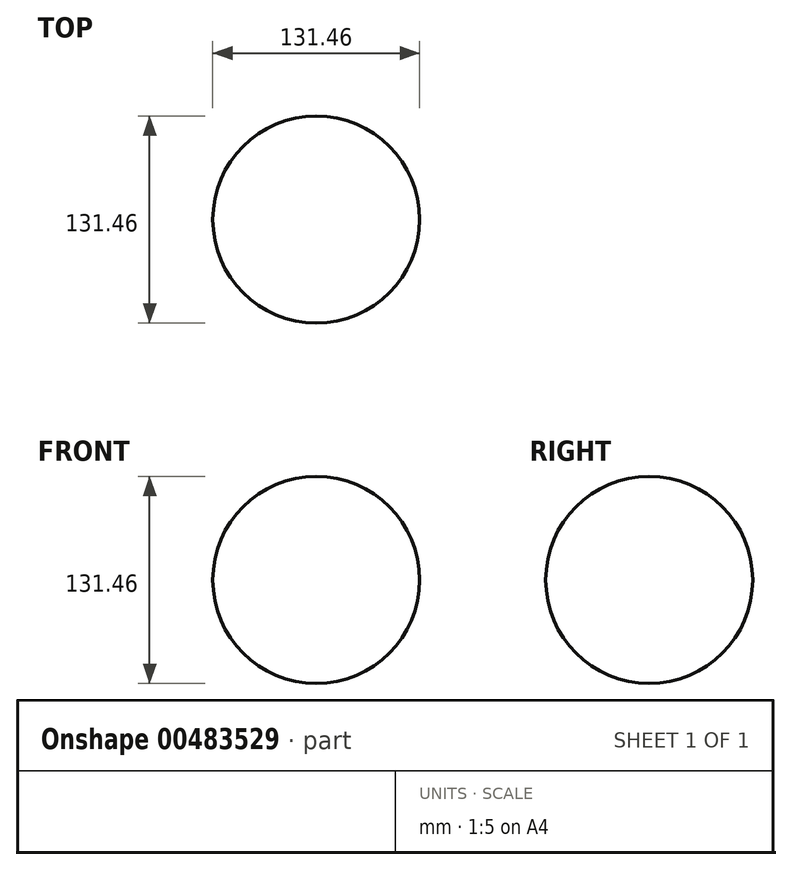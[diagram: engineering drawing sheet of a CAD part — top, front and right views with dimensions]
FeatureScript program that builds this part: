
annotation { "Feature Type Name" : "Feature", "Feature Type Description" : "" }
export const myFeature = defineFeature(function(context is Context, id is Id, definition is map)
    precondition{}
    {
        {
            var Q0;
            Q0=qCreatedBy(makeId("Right.planeOp"),FACE);
            var sketch = newSketch(context, id + "F0", { "sketchPlane" : qUnion([Q0])});
            skCircle(sketch, "E0", {"center": v(0, 0) * mm, "radius": 65.73 * mm});
            skLineSegment(sketch, "E1", {"start": v(0, 69.96) * mm, "end": v(0, -70.53) * mm});
            skSolve(sketch);
        }
        {
            var Q0;
            {var subQ0=sQuery(id+"F0.wireOp",EDGE,"E1");var subQ1=sQuery(id+"F0.wireOp",EDGE,"E0");var subQ2=makeQuery(id+"F0.imprint","INTERSECT",VERTEX,{"disambiguationData":[OD(0.0)],"derivedFrom":[subQ1,subQ0]});Q0=makeQuery(id+"F0.imprint","IMPRINT",FACE,{"disambiguationData":[TD([[makeQuery(id+"F0.imprint","IMPRINT",EDGE,{"disambiguationData":[TD([[subQ2,1.0]])],"derivedFrom":subQ1}),1.0]])]});}
            var Q1;
            Q1=sQuery(id+"F0.wireOp",EDGE,"E1");
            revolve(context, id + "F1", {"entities" : qUnion([Q0]), "axis" : qUnion([Q1]), "revolveType" : RevolveType.FULL});
        }
    });
